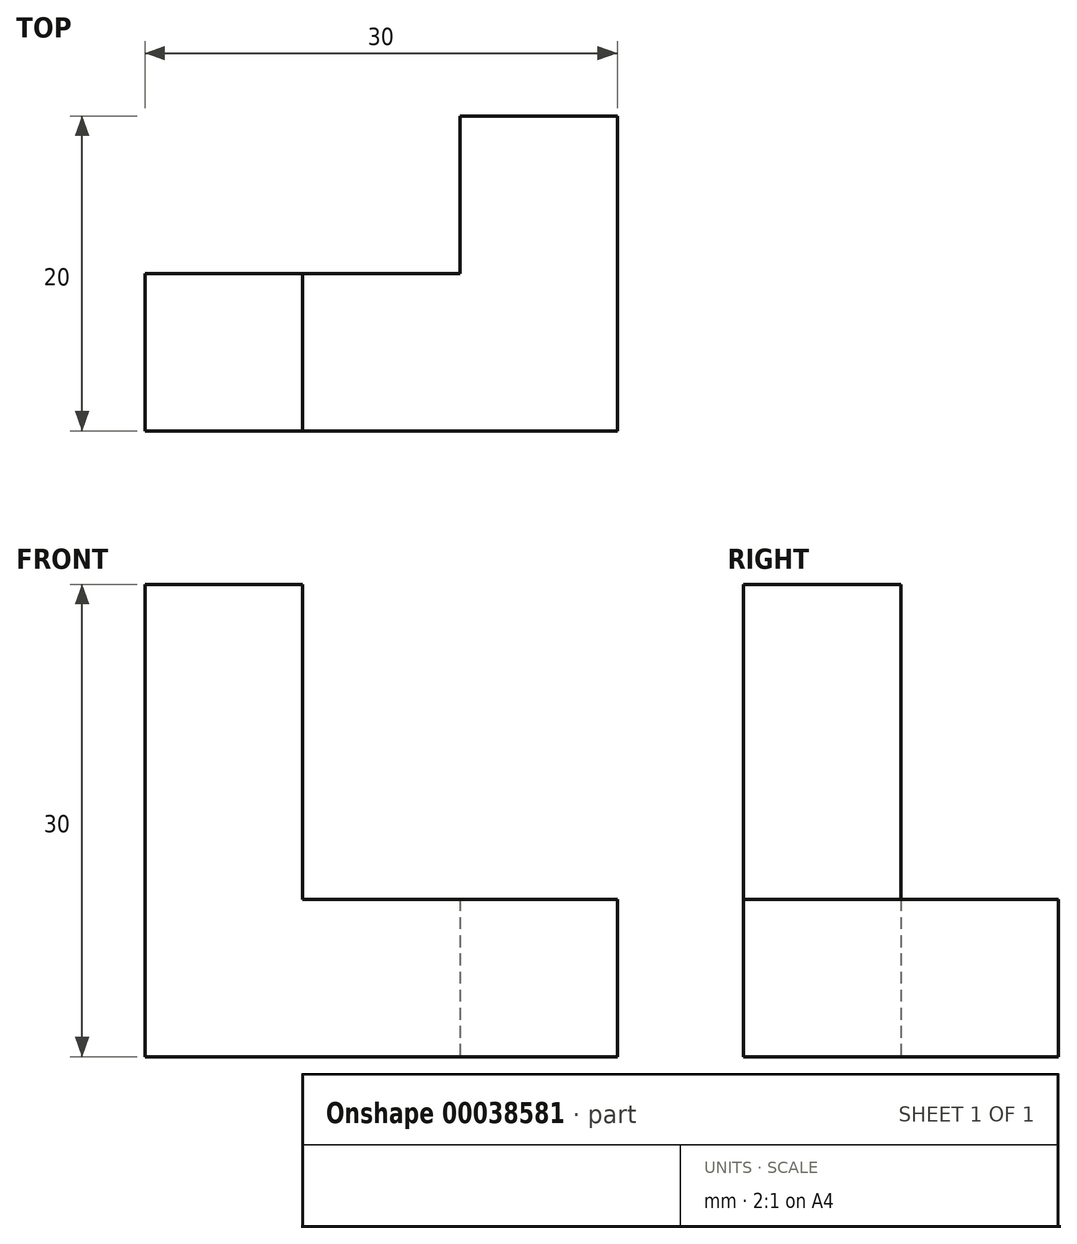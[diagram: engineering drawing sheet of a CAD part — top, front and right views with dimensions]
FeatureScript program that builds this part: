
annotation { "Feature Type Name" : "Feature", "Feature Type Description" : "" }
export const myFeature = defineFeature(function(context is Context, id is Id, definition is map)
    precondition{}
    {
        {
            var Q0;
            Q0=qCreatedBy(makeId("Top.planeOp"),FACE);
            var sketch = newSketch(context, id + "F0", { "sketchPlane" : qUnion([Q0])});
            skLineSegment(sketch, "E0.bottom", {"start": v(0, 0) * mm, "end": v(10, 0) * mm});
            skLineSegment(sketch, "E0.top", {"start": v(0, 10) * mm, "end": v(10, 10) * mm});
            skLineSegment(sketch, "E0.left", {"start": v(0, 0) * mm, "end": v(0, 10) * mm});
            skLineSegment(sketch, "E0.right", {"start": v(10, 0) * mm, "end": v(10, 10) * mm});
            skSolve(sketch);
        }
        {
            var Q0;
            Q0 = qSketchRegion(id + "F0", true);
            extrude(context, id + "F1", {"entities" : qUnion([Q0]), "depth" : 30 * mm});
        }
        {
            var Q0;
            Q0=makeQuery(id+"F1.opExtrude","SWEPT_FACE",FACE,{"disambiguationData":[OSD([sQuery(id+"F0.wireOp",EDGE,"E0.right")])]});
            var sketch = newSketch(context, id + "F2", { "sketchPlane" : qUnion([Q0])});
            skLineSegment(sketch, "E1.bottom", {"start": v(0, 0) * mm, "end": v(10, 0) * mm});
            skLineSegment(sketch, "E1.top", {"start": v(0, 10) * mm, "end": v(10, 10) * mm});
            skLineSegment(sketch, "E1.left", {"start": v(0, 0) * mm, "end": v(0, 10) * mm});
            skLineSegment(sketch, "E1.right", {"start": v(10, 0) * mm, "end": v(10, 10) * mm});
            skSolve(sketch);
        }
        {
            var Q0;
            Q0 = qSketchRegion(id + "F2", true);
            extrude(context, id + "F3", {"entities" : qUnion([Q0]), "operationType" : NewBodyOperationType.ADD, "depth" : 20 * mm});
        }
        {
            var Q0;
            Q0=makeQuery(id+"F3.boolean.opBoolean","MERGE",FACE,{"derivedFrom":[makeQuery(id+"F1.opExtrude","SWEPT_FACE",FACE,{"disambiguationData":[OSD([sQuery(id+"F0.wireOp",EDGE,"E0.top")])]}),makeQuery(id+"F3.opExtrude","SWEPT_FACE",FACE,{"disambiguationData":[OSD([sQuery(id+"F2.wireOp",EDGE,"E1.right")])]})]});
            var sketch = newSketch(context, id + "F4", { "sketchPlane" : qUnion([Q0])});
            skLineSegment(sketch, "E2.bottom", {"start": v(-30, 10) * mm, "end": v(-20, 10) * mm});
            skLineSegment(sketch, "E2.top", {"start": v(-30, 0) * mm, "end": v(-20, 0) * mm});
            skLineSegment(sketch, "E2.left", {"start": v(-30, 10) * mm, "end": v(-30, 0) * mm});
            skLineSegment(sketch, "E2.right", {"start": v(-20, 10) * mm, "end": v(-20, 0) * mm});
            skSolve(sketch);
        }
        {
            var Q0;
            Q0 = qSketchRegion(id + "F4", true);
            extrude(context, id + "F5", {"entities" : qUnion([Q0]), "operationType" : NewBodyOperationType.ADD, "depth" : 10 * mm});
        }
    });
